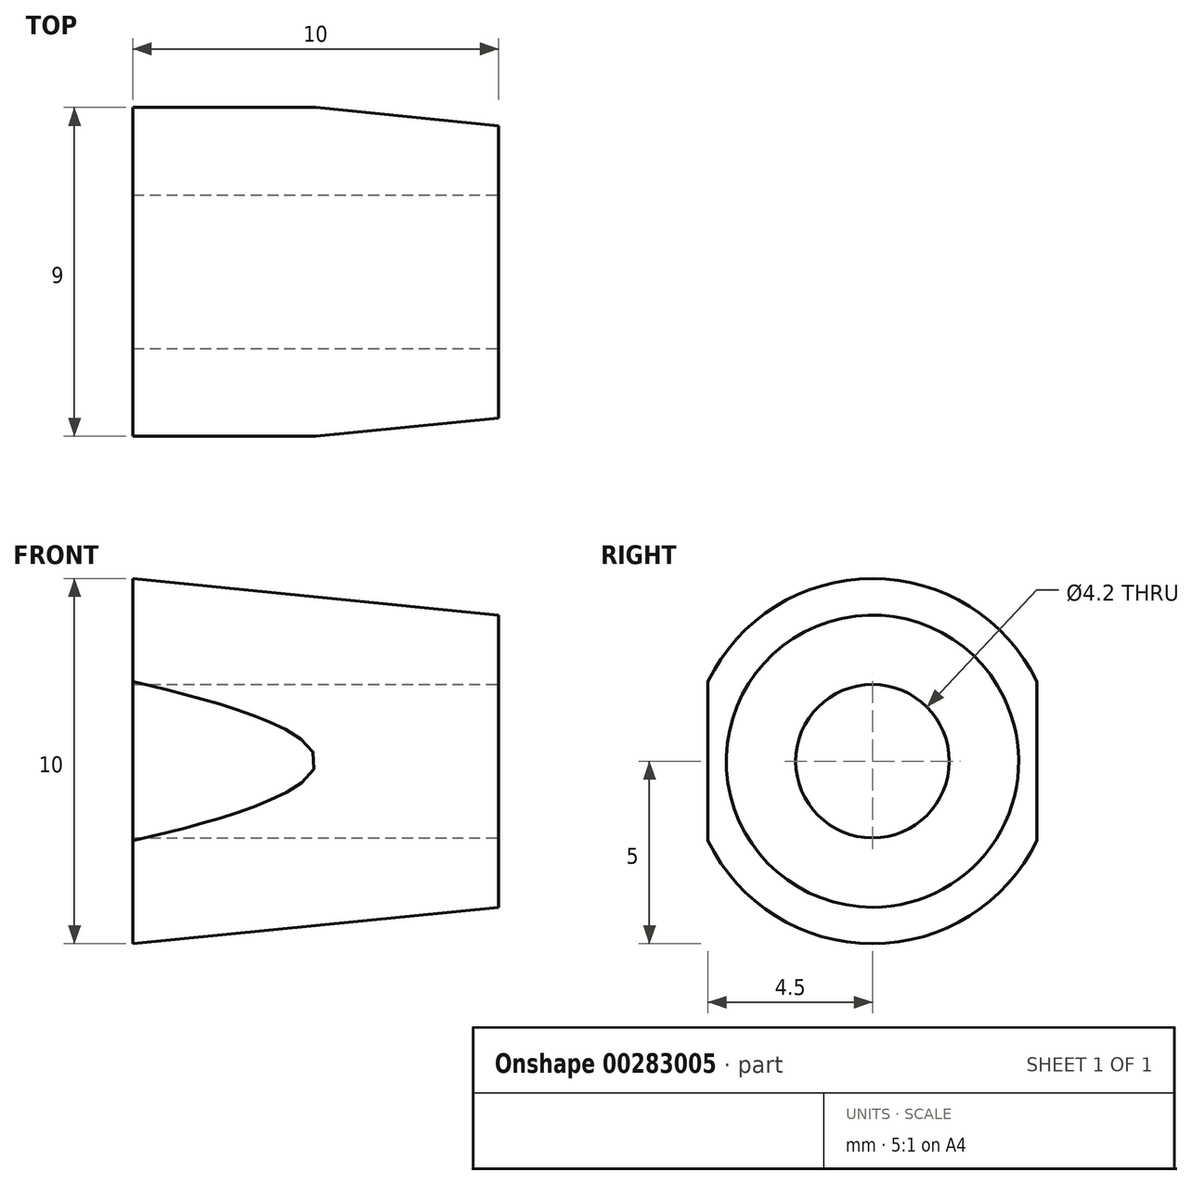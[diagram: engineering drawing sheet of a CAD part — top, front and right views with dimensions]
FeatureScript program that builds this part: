
annotation { "Feature Type Name" : "Feature", "Feature Type Description" : "" }
export const myFeature = defineFeature(function(context is Context, id is Id, definition is map)
    precondition{}
    {
        {
            var Q0;
            Q0=qCreatedBy(makeId("Front.planeOp"),FACE);
            var sketch = newSketch(context, id + "F0", { "sketchPlane" : qUnion([Q0])});
            skLineSegment(sketch, "E0", {"start": v(0, 0) * mm, "end": v(-10, 0) * mm});
            skLineSegment(sketch, "E1", {"start": v(-10, 0) * mm, "end": v(-10, 5) * mm});
            skLineSegment(sketch, "E2", {"start": v(-10, 5) * mm, "end": v(0, 4) * mm});
            skLineSegment(sketch, "E3", {"start": v(0, 4) * mm, "end": v(0, 0) * mm});
            skSolve(sketch);
        }
        {
            var Q0;
            Q0=makeQuery(id+"F0.imprint","IMPRINT",FACE,{"disambiguationData":[TD([[makeQuery(id+"F0.imprint","IMPRINT",EDGE,{"derivedFrom":sQuery(id+"F0.wireOp",EDGE,"E0")}),-1.0]])]});
            var Q1;
            Q1=sQuery(id+"F0.wireOp",EDGE,"E0");
            revolve(context, id + "F1", {"entities" : qUnion([Q0]), "axis" : qUnion([Q1]), "revolveType" : RevolveType.FULL});
        }
        {
            var Q0;
            Q0=makeQuery(id+"F1.opRevolve","SWEPT_FACE",FACE,{"disambiguationData":[OSD([sQuery(id+"F0.wireOp",EDGE,"E3")])]});
            var sketch = newSketch(context, id + "F2", { "sketchPlane" : qUnion([Q0])});
            skLineSegment(sketch, "E4", {"start": v(-4.5, 7.5) * mm, "end": v(-4.5, -7.5) * mm});
            skLineSegment(sketch, "E5", {"start": v(-4.5, -7.5) * mm, "end": v(4.5, -7.5) * mm});
            skLineSegment(sketch, "E6", {"start": v(4.5, -7.5) * mm, "end": v(4.5, 7.5) * mm});
            skLineSegment(sketch, "E7", {"start": v(4.5, 7.5) * mm, "end": v(-4.5, 7.5) * mm});
            skLineSegment(sketch, "E8", {"start": v(0, 0) * mm, "end": v(12, 0) * mm, "construction": true});
            skLineSegment(sketch, "E9", {"start": v(0, 0) * mm, "end": v(0, 13.4) * mm, "construction": true});
            skSolve(sketch);
        }
        {
            var Q0;
            Q0=qSketchRegion(id+"F2",true);
            extrude(context, id + "F3", {"entities" : qUnion([Q0]), "operationType" : NewBodyOperationType.INTERSECT, "endBound" : BoundingType.THROUGH_ALL, "oppositeDirection" : true, "depth" : 25 * mm});
        }
        {
            var Q0;
            Q0=makeQuery(id+"F1.opRevolve","SWEPT_FACE",FACE,{"disambiguationData":[OSD([sQuery(id+"F0.wireOp",EDGE,"E3")])]});
            var sketch = newSketch(context, id + "F4", { "sketchPlane" : qUnion([Q0])});
            skPoint(sketch, "E10", {"position": v(0, 0) * mm});
            skSolve(sketch);
        }
        {
            var Q0;
            Q0=sQuery(id+"F4.wireOp",VERTEX,"E10");
            var Q1;
            Q1=makeQuery(id+"F1.opRevolve","SWEPT_BODY",BODY,{"disambiguationData":[OSD([sQuery(id+"F0.wireOp",EDGE,"E0"),sQuery(id+"F0.wireOp",EDGE,"E1"),sQuery(id+"F0.wireOp",EDGE,"E2"),sQuery(id+"F0.wireOp",EDGE,"E3")])]});
            hole(context, id + "F5", {"style" : HoleStyle.SIMPLE, "endStyle" : HoleEndStyle.THROUGH, "standardTappedOrClearance" : lookupTablePath({ "standard" : "ISO", "engagement" : "75%", "pitch" : "0.8 mm", "size" : "M5", "type" : "Tapped" }), "standardBlindInLast" : lookupTablePath({ "standard" : "ISO", "engagement" : "75%", "pitch" : "0.8 mm", "size" : "M5", "type" : "Tapped" }), "holeDiameter" : 4.2 * mm, "showTappedDepth" : true, "tappedDepth" : 12 * mm, "tapClearance" : 3, "locations" : qUnion([Q0]), "scope" : qUnion([Q1]), "majorDiameter" : 5 * mm});
        }
    });
